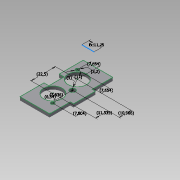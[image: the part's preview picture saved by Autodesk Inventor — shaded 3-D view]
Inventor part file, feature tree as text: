
AUTODESK INVENTOR PART (.ipt)
format: ipt  version: 2015 SP1 (Build 190203100, 203)  size: 124,928 bytes
history: native  units: mm
features: sketch x2, extrude x1, projected_geometry x1
ambient origin geometry x8: Origin, YZ Plane, XZ Plane, XY Plane, X Axis, Y Axis, Z Axis, Center Point
bodies: Body1 (feature_tree)
feature tree (4):
  extrude  "Extrusion2"  Depth=58.0mm
  sketch  "Sketch2"  dims[d3=10.0mm d4=3.0mm d5=20.0mm d10=8.0mm d11=7.0mm d12=14.0mm d13=3.0mm d14=0.0mm d15=17.0mm d16=3.2mm d17=5.0mm d18=22.5mm d19=7.654mm d20=7.654mm d21=7.635648mm d22=7.803528mm d23=6.539634mm d24=11.5345mm d25=10.9655mm d26=11.25mm]
  sketch  "Sketch1"  dims[d1=29.0mm d2=58.0mm]
  projected_geometry  "Projected Loop1"
